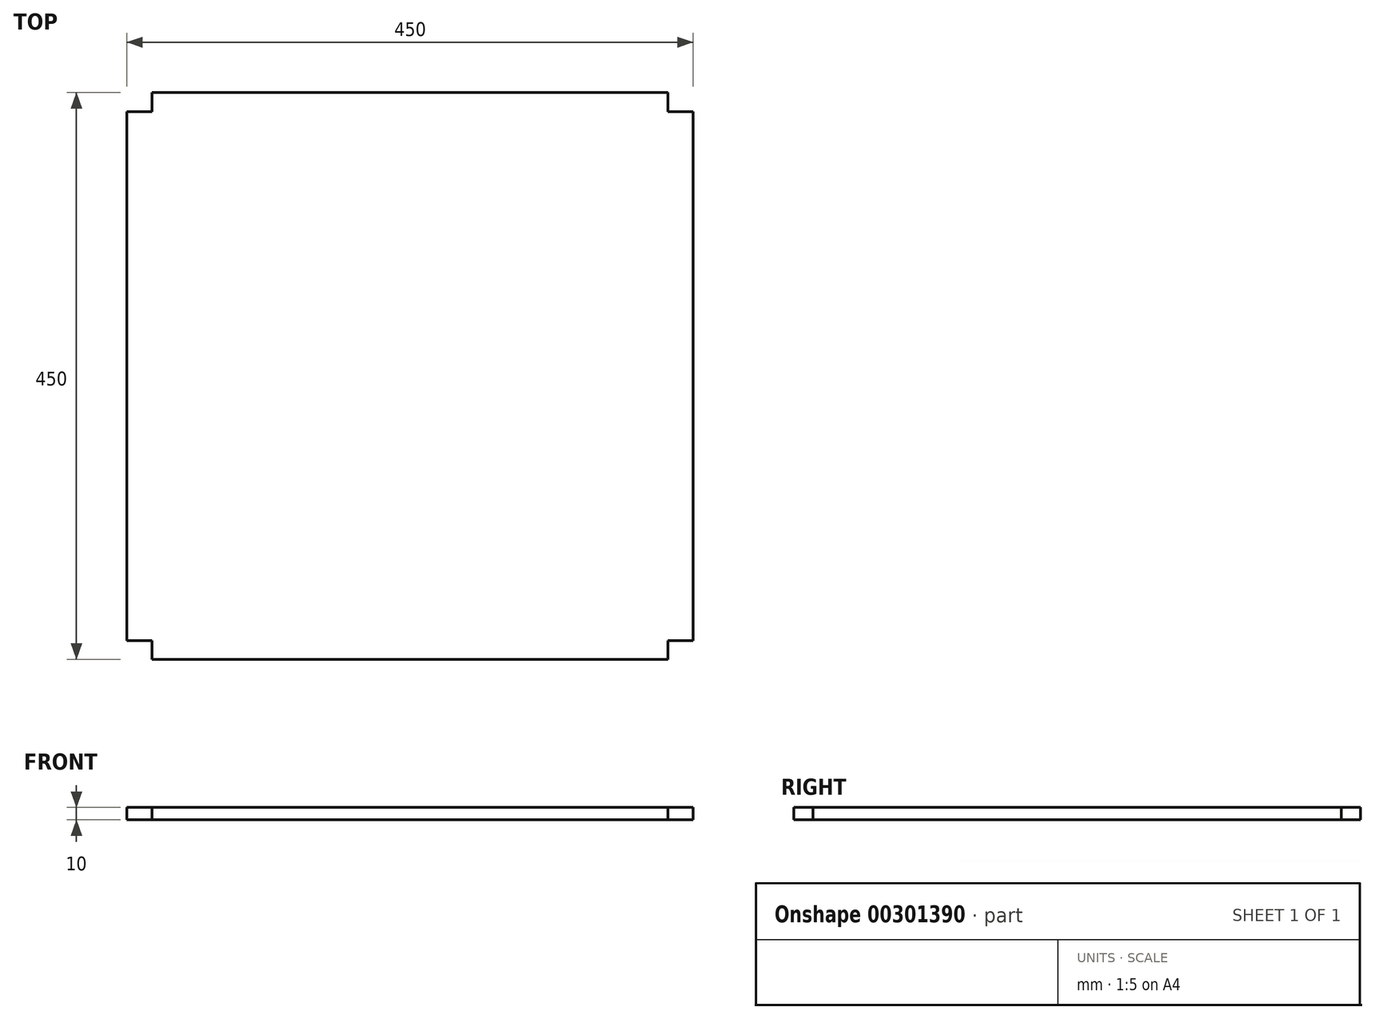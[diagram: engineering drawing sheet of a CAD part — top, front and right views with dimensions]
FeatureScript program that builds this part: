
annotation { "Feature Type Name" : "Feature", "Feature Type Description" : "" }
export const myFeature = defineFeature(function(context is Context, id is Id, definition is map)
    precondition{}
    {
        {
            var Q0;
            Q0=qCreatedBy(makeId("Top.planeOp"),FACE);
            var sketch = newSketch(context, id + "F0", { "sketchPlane" : qUnion([Q0])});
            skLineSegment(sketch, "E0.bottom", {"start": v(0, 0) * mm, "end": v(450, 0) * mm});
            skLineSegment(sketch, "E0.top", {"start": v(0, -450) * mm, "end": v(450, -450) * mm});
            skLineSegment(sketch, "E0.left", {"start": v(0, 0) * mm, "end": v(0, -450) * mm});
            skLineSegment(sketch, "E0.right", {"start": v(450, 0) * mm, "end": v(450, -450) * mm});
            skSolve(sketch);
        }
        {
            var Q0;
            Q0=makeQuery(id+"F0.imprint","IMPRINT",FACE,{"disambiguationData":[TD([[makeQuery(id+"F0.imprint","IMPRINT",EDGE,{"derivedFrom":sQuery(id+"F0.wireOp",EDGE,"E0.bottom")}),-1.0]])]});
            extrude(context, id + "F1", {"entities" : qUnion([Q0]), "depth" : 10 * mm});
        }
        {
            var Q0;
            Q0=makeQuery(id+"F1.opExtrude","CAP_FACE",FACE,{"disambiguationData":[OSD([sQuery(id+"F0.wireOp",EDGE,"E0.bottom"),sQuery(id+"F0.wireOp",EDGE,"E0.top"),sQuery(id+"F0.wireOp",EDGE,"E0.left"),sQuery(id+"F0.wireOp",EDGE,"E0.right")])],"isStart":false});
            var sketch = newSketch(context, id + "F2", { "sketchPlane" : qUnion([Q0])});
            skLineSegment(sketch, "E1.bottom", {"start": v(0, 0) * mm, "end": v(20, 0) * mm});
            skLineSegment(sketch, "E1.top", {"start": v(0, -15) * mm, "end": v(20, -15) * mm});
            skLineSegment(sketch, "E1.left", {"start": v(0, 0) * mm, "end": v(0, -15) * mm});
            skLineSegment(sketch, "E1.right", {"start": v(20, 0) * mm, "end": v(20, -15) * mm});
            skLineSegment(sketch, "E2.bottom", {"start": v(0, -450) * mm, "end": v(20, -450) * mm});
            skLineSegment(sketch, "E2.top", {"start": v(0, -435) * mm, "end": v(20, -435) * mm});
            skLineSegment(sketch, "E2.left", {"start": v(0, -450) * mm, "end": v(0, -435) * mm});
            skLineSegment(sketch, "E2.right", {"start": v(20, -450) * mm, "end": v(20, -435) * mm});
            skLineSegment(sketch, "E3.bottom", {"start": v(450, 0) * mm, "end": v(430, 0) * mm});
            skLineSegment(sketch, "E3.top", {"start": v(450, -15) * mm, "end": v(430, -15) * mm});
            skLineSegment(sketch, "E3.left", {"start": v(450, 0) * mm, "end": v(450, -15) * mm});
            skLineSegment(sketch, "E3.right", {"start": v(430, 0) * mm, "end": v(430, -15) * mm});
            skLineSegment(sketch, "E4.bottom", {"start": v(450, -450) * mm, "end": v(430, -450) * mm});
            skLineSegment(sketch, "E4.top", {"start": v(450, -435) * mm, "end": v(430, -435) * mm});
            skLineSegment(sketch, "E4.left", {"start": v(450, -450) * mm, "end": v(450, -435) * mm});
            skLineSegment(sketch, "E4.right", {"start": v(430, -450) * mm, "end": v(430, -435) * mm});
            skSolve(sketch);
        }
        {
            var Q0;
            Q0=makeQuery(id+"F2.imprint","IMPRINT",FACE,{"disambiguationData":[TD([[makeQuery(id+"F2.imprint","IMPRINT",EDGE,{"derivedFrom":sQuery(id+"F2.wireOp",EDGE,"E3.bottom")}),-1.0]])]});
            var Q1;
            Q1=makeQuery(id+"F2.imprint","IMPRINT",FACE,{"disambiguationData":[TD([[makeQuery(id+"F2.imprint","IMPRINT",EDGE,{"derivedFrom":sQuery(id+"F2.wireOp",EDGE,"E1.bottom")}),-1.0]])]});
            var Q2;
            Q2=makeQuery(id+"F2.imprint","IMPRINT",FACE,{"disambiguationData":[TD([[makeQuery(id+"F2.imprint","IMPRINT",EDGE,{"derivedFrom":sQuery(id+"F2.wireOp",EDGE,"E2.bottom")}),1.0]])]});
            var Q3;
            Q3=makeQuery(id+"F2.imprint","IMPRINT",FACE,{"disambiguationData":[TD([[makeQuery(id+"F2.imprint","IMPRINT",EDGE,{"derivedFrom":sQuery(id+"F2.wireOp",EDGE,"E4.bottom")}),1.0]])]});
            extrude(context, id + "F3", {"entities" : qUnion([Q0, Q1, Q2, Q3]), "operationType" : NewBodyOperationType.REMOVE, "endBound" : BoundingType.THROUGH_ALL, "oppositeDirection" : true, "depth" : 25 * mm});
        }
        {
            var Q0;
            Q0=makeQuery(id+"F1.opExtrude","SWEPT_BODY",BODY,{"disambiguationData":[OSD([sQuery(id+"F0.wireOp",EDGE,"E0.bottom"),sQuery(id+"F0.wireOp",EDGE,"E0.top"),sQuery(id+"F0.wireOp",EDGE,"E0.left"),sQuery(id+"F0.wireOp",EDGE,"E0.right")])]});
            transform(context, id + "F4", {"entities" : qUnion([Q0]), "transformType" : TransformType.TRANSLATION_3D, "dx" : 0 * mm, "dy" : 0 * mm, "dz" : 0 * mm, "makeCopy" : true});
        }
    });
